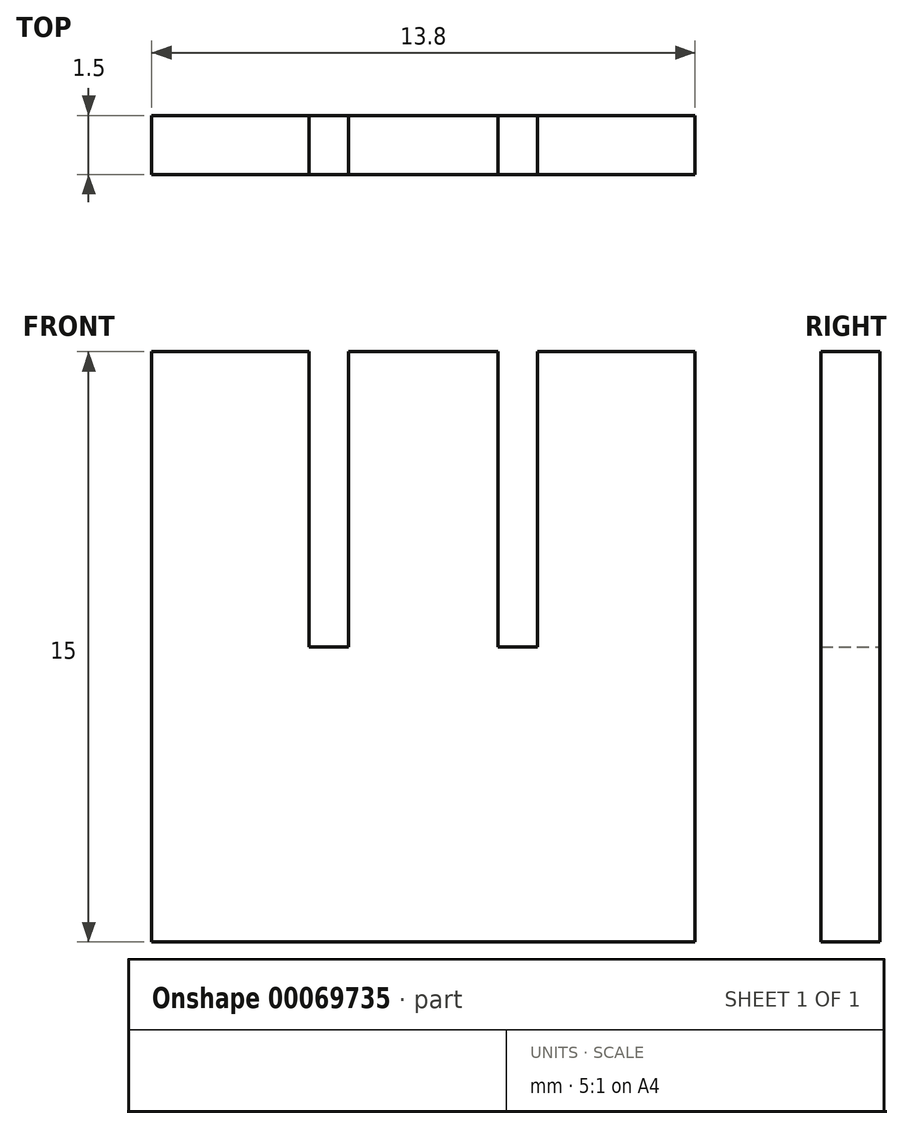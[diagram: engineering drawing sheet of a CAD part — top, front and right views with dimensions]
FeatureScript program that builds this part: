
annotation { "Feature Type Name" : "Feature", "Feature Type Description" : "" }
export const myFeature = defineFeature(function(context is Context, id is Id, definition is map)
    precondition{}
    {
        {
            var Q0;
            Q0=qCreatedBy(makeId("Front.planeOp"),FACE);
            var sketch = newSketch(context, id + "F0", { "sketchPlane" : qUnion([Q0])});
            skLineSegment(sketch, "E0.top", {"start": v(-6.9, -7.5) * mm, "end": v(6.9, -7.5) * mm});
            skLineSegment(sketch, "E0.left", {"start": v(-6.9, 7.5) * mm, "end": v(-6.9, -7.5) * mm});
            skLineSegment(sketch, "E0.right", {"start": v(6.9, 7.5) * mm, "end": v(6.9, -7.5) * mm});
            skLineSegment(sketch, "E1", {"start": v(6.9, 7.5) * mm, "end": v(2.9, 7.5) * mm});
            skLineSegment(sketch, "E2", {"start": v(2.9, 7.5) * mm, "end": v(2.9, 0) * mm});
            skLineSegment(sketch, "E3", {"start": v(2.9, 0) * mm, "end": v(1.9, 0) * mm});
            skLineSegment(sketch, "E4", {"start": v(1.9, 0) * mm, "end": v(1.9, 7.5) * mm});
            skLineSegment(sketch, "E5", {"start": v(1.9, 7.5) * mm, "end": v(-1.9, 7.5) * mm});
            skLineSegment(sketch, "E6", {"start": v(-1.9, 7.5) * mm, "end": v(-1.9, 0) * mm});
            skLineSegment(sketch, "E7", {"start": v(-1.9, 0) * mm, "end": v(-2.9, 0) * mm});
            skLineSegment(sketch, "E8", {"start": v(-2.9, 0) * mm, "end": v(-2.9, 7.5) * mm});
            skLineSegment(sketch, "E9", {"start": v(-2.9, 7.5) * mm, "end": v(-6.9, 7.5) * mm});
            skSolve(sketch);
        }
        {
            var Q0;
            Q0 = qSketchRegion(id + "F0", true);
            extrude(context, id + "F1", {"entities" : qUnion([Q0]), "depth" : 1.5 * mm});
        }
    });
